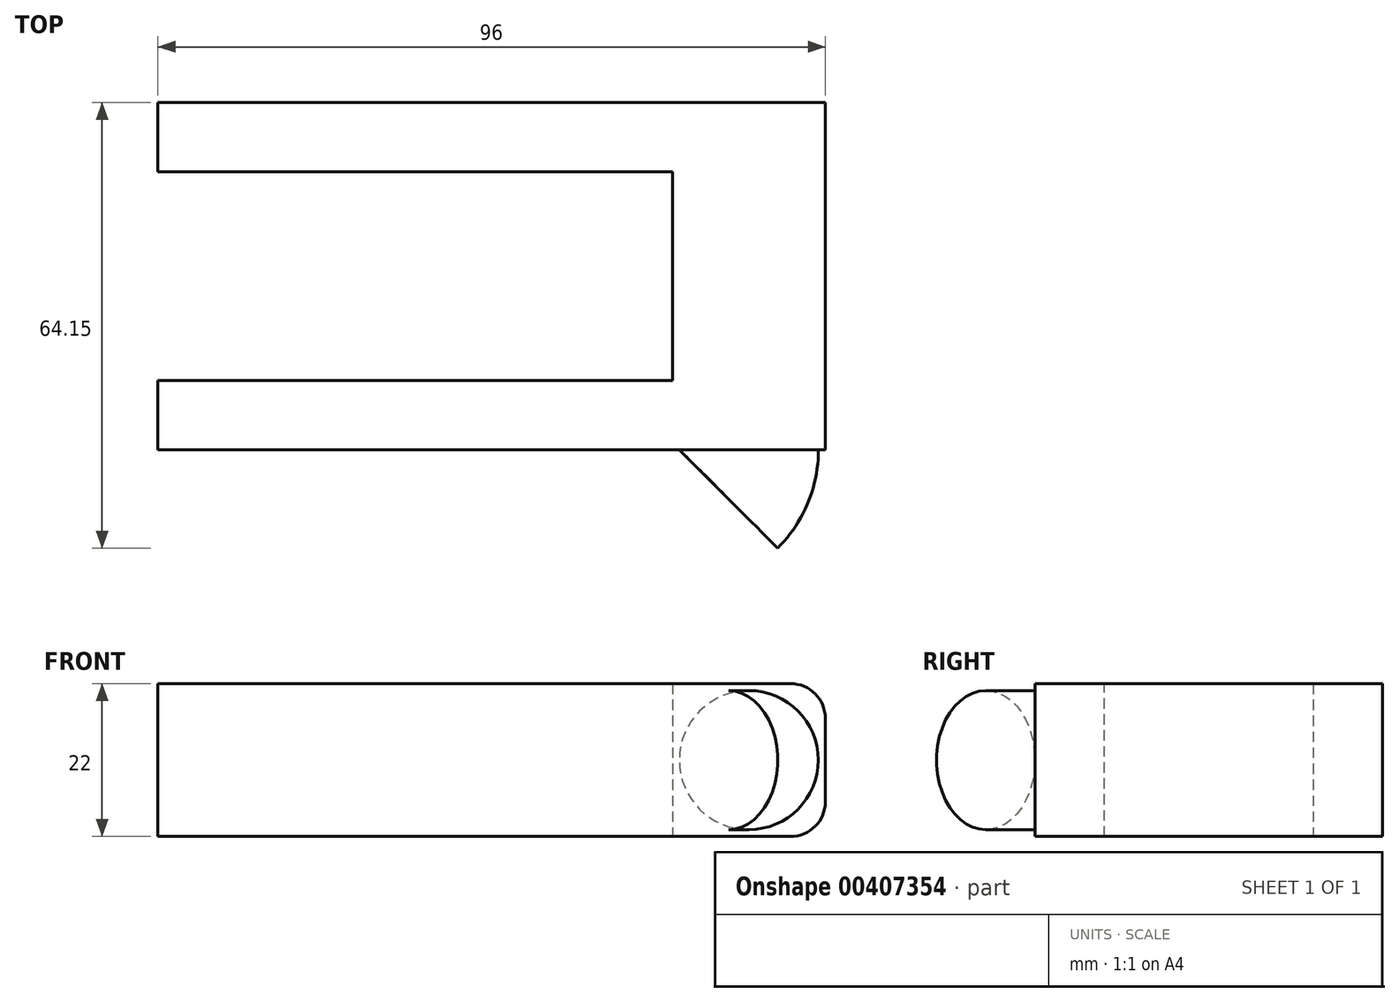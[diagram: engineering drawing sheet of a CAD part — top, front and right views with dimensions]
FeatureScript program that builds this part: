
annotation { "Feature Type Name" : "Feature", "Feature Type Description" : "" }
export const myFeature = defineFeature(function(context is Context, id is Id, definition is map)
    precondition{}
    {
        {
            var Q0;
            Q0=qCreatedBy(makeId("Front.planeOp"),FACE);
            var sketch = newSketch(context, id + "F0", { "sketchPlane" : qUnion([Q0])});
            skCircle(sketch, "E0", {"center": v(0, 0) * mm, "radius": 10 * mm});
            skSolve(sketch);
        }
        {
            var Q0;
            Q0=qCreatedBy(makeId("Front.planeOp"),FACE);
            var sketch = newSketch(context, id + "F1", { "sketchPlane" : qUnion([Q0])});
            skLineSegment(sketch, "E1", {"start": v(-10, 7.92) * mm, "end": v(-10, -9.36) * mm});
            skSolve(sketch);
        }
        {
            var Q0;
            Q0=makeQuery(id+"F0.imprint","IMPRINT",FACE,{"disambiguationData":[TD([[makeQuery(id+"F0.imprint","IMPRINT",EDGE,{"derivedFrom":sQuery(id+"F0.wireOp",EDGE,"E0")}),1.0]])]});
            var Q1;
            Q1=sQuery(id+"F1.wireOp",EDGE,"E1");
            revolve(context, id + "F2", {"entities" : qUnion([Q0]), "axis" : qUnion([Q1]), "revolveType" : RevolveType.ONE_DIRECTION, "angle" : 45 * degree});
        }
        {
            var Q0;
            Q0=makeQuery(id+"F2.opRevolve","CAP_FACE",FACE,{"disambiguationData":[OSD([sQuery(id+"F0.wireOp",EDGE,"E0")])],"isStart":true});
            var sketch = newSketch(context, id + "F3", { "sketchPlane" : qUnion([Q0])});
            skLineSegment(sketch, "E2.bottom", {"start": v(-11, 11) * mm, "end": v(11, 11) * mm});
            skLineSegment(sketch, "E2.top", {"start": v(-11, -11) * mm, "end": v(11, -11) * mm});
            skLineSegment(sketch, "E2.left", {"start": v(-11, 11) * mm, "end": v(-11, -11) * mm});
            skLineSegment(sketch, "E2.right", {"start": v(11, 11) * mm, "end": v(11, -11) * mm});
            skPoint(sketch, "E2.middle", {"position": v(0, 0) * mm});
            skSolve(sketch);
        }
        {
            var Q0;
            Q0=makeQuery(id+"F3.imprint","IMPRINT",FACE,{"disambiguationData":[TD([[makeQuery(id+"F3.imprint","IMPRINT",EDGE,{"derivedFrom":sQuery(id+"F3.wireOp",EDGE,"E2.bottom")}),-1.0]])]});
            var Q1;
            Q1=makeQuery(id+"F3.imprint","IMPRINT",FACE,{"disambiguationData":[TD([[makeQuery(id+"F3.imprint","IMPRINT",EDGE,{"derivedFrom":makeQuery(id+"F2.opRevolve","CAP_EDGE",EDGE,{"disambiguationData":[OSD([sQuery(id+"F0.wireOp",EDGE,"E0")])],"isStart":true})}),-1.0]])]});
            extrude(context, id + "F4", {"entities" : qUnion([Q0, Q1]), "operationType" : NewBodyOperationType.ADD, "depth" : 50 * mm});
        }
        {
            var Q0;
            Q0=makeQuery(id+"F4.opExtrude","SWEPT_FACE",FACE,{"disambiguationData":[OSD([sQuery(id+"F3.wireOp",EDGE,"E2.right")])]});
            var sketch = newSketch(context, id + "F5", { "sketchPlane" : qUnion([Q0])});
            skLineSegment(sketch, "E3.bottom", {"start": v(0, 11) * mm, "end": v(0, 11) * mm});
            skLineSegment(sketch, "E3.top", {"start": v(0, -11) * mm, "end": v(0, -11) * mm});
            skLineSegment(sketch, "E3.left", {"start": v(0, 11) * mm, "end": v(0, -11) * mm});
            skLineSegment(sketch, "E3.right", {"start": v(0, 11) * mm, "end": v(0, -11) * mm});
            skLineSegment(sketch, "E4.bottom", {"start": v(0, 11) * mm, "end": v(-10, 11) * mm});
            skLineSegment(sketch, "E4.top", {"start": v(0, 11) * mm, "end": v(-10, 11) * mm});
            skLineSegment(sketch, "E4.right", {"start": v(-10, 11) * mm, "end": v(-10, 11) * mm});
            skLineSegment(sketch, "E5.bottom", {"start": v(-10, -11) * mm, "end": v(0, -11) * mm});
            skLineSegment(sketch, "E5.top", {"start": v(-10, 11) * mm, "end": v(0, 11) * mm});
            skLineSegment(sketch, "E5.left", {"start": v(-10, -11) * mm, "end": v(-10, 11) * mm});
            skLineSegment(sketch, "E5.right", {"start": v(0, -11) * mm, "end": v(0, 11) * mm});
            skSolve(sketch);
        }
        {
            var Q0;
            Q0=makeQuery(id+"F5.imprint","IMPRINT",FACE,{"disambiguationData":[TD([[makeQuery(id+"F5.imprint","IMPRINT",EDGE,{"derivedFrom":sQuery(id+"F5.wireOp",EDGE,"E5.bottom")}),1.0]])]});
            extrude(context, id + "F6", {"entities" : qUnion([Q0]), "operationType" : NewBodyOperationType.ADD, "depth" : 74 * mm});
        }
        {
            var Q0;
            Q0=makeQuery(id+"F4.opExtrude","SWEPT_FACE",FACE,{"disambiguationData":[OSD([sQuery(id+"F3.wireOp",EDGE,"E2.right")])]});
            var sketch = newSketch(context, id + "F7", { "sketchPlane" : qUnion([Q0])});
            skLineSegment(sketch, "E6.bottom", {"start": v(-50, 11) * mm, "end": v(-40, 11) * mm});
            skLineSegment(sketch, "E6.top", {"start": v(-50, -11) * mm, "end": v(-40, -11) * mm});
            skLineSegment(sketch, "E6.left", {"start": v(-50, 11) * mm, "end": v(-50, -11) * mm});
            skLineSegment(sketch, "E6.right", {"start": v(-40, 11) * mm, "end": v(-40, -11) * mm});
            skSolve(sketch);
        }
        {
            var Q0;
            Q0=makeQuery(id+"F7.imprint","IMPRINT",FACE,{"disambiguationData":[TD([[makeQuery(id+"F7.imprint","IMPRINT",EDGE,{"derivedFrom":sQuery(id+"F7.wireOp",EDGE,"E6.bottom")}),-1.0]])]});
            extrude(context, id + "F8", {"entities" : qUnion([Q0]), "operationType" : NewBodyOperationType.ADD, "depth" : 74 * mm});
        }
        {
            var Q0;
            Q0=makeQuery(id+"F4.opExtrude","SWEPT_EDGE",EDGE,{"disambiguationData":[OSD([sQuery(id+"F3.wireOp",EDGE,"E2.top"),sQuery(id+"F3.wireOp",EDGE,"E2.left")])]});
            var Q1;
            Q1=makeQuery(id+"F4.opExtrude","SWEPT_EDGE",EDGE,{"disambiguationData":[OSD([sQuery(id+"F3.wireOp",EDGE,"E2.bottom"),sQuery(id+"F3.wireOp",EDGE,"E2.left")])]});
            fillet(context, id + "F9", {"entities" : qUnion([Q0, Q1]), "radius" : 5 * mm, "tangentPropagation" : true, "allowEdgeOverflow" : false});
        }
    });
